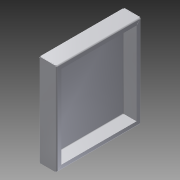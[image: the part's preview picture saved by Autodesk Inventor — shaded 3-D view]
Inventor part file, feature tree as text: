
AUTODESK INVENTOR PART (.ipt)
format: ipt  version: 2015 (Build 190159000, 159)  size: 343,552 bytes
history: native  units: mm
features: sheet_metal_op x11, other x5, sketch x3
ambient origin geometry x8: Origin, YZ Plane, XZ Plane, XY Plane, X Axis, Y Axis, Z Axis, Center Point
bodies: Solid1 (feature_tree)
feature tree (19):
  sheet_metal_op  "Face1"
  sheet_metal_op  "Flange1"
  other  "A-Side Definition"
  sheet_metal_op  "Flange3"
  sketch  "Sketch1"  dims[d0=220.0mm]
  other  "Plate1"
  sketch  "Sketch2"  dims[d1=240.0mm]
  other  "Plate2"
  sheet_metal_op  "Bend1"
  sheet_metal_op  "Corner1"
  sketch  "Sketch4"  dims[d2=1.6mm d3=1.6mm d4=0.8mm d5=3.2mm d6=1.6mm d7=47.0mm d8=90.0deg d9=1.6mm d10=6.4mm d11=1.6mm d12=1.6mm d33=6.4mm d34=1.6mm d35=0.1mm d36=0.0mm d37=10.0mm d38=6.4mm d39=1.6mm d40=0.1mm d41=0.0mm d42=10.0mm d43=6.4mm d44=1.6mm d45=0.1mm d46=0.0mm d47=10.0mm d48=6.4mm d49=1.6mm d50=0.1mm d51=0.0mm d52=10.0mm d53=1.6mm d54=0.8mm d55=3.2mm d56=1.6mm d57=12.0mm d58=90.0deg d59=1.6mm d60=6.4mm d61=0.1mm d62=1.6mm]
  other  "Plate4"
  sheet_metal_op  "Bend3"
  sheet_metal_op  "Corner3"
  sheet_metal_op  "Corner5"
  sheet_metal_op  "Corner6"
  sheet_metal_op  "Corner7"
  sheet_metal_op  "Corner8"
  other  "Definition1"
